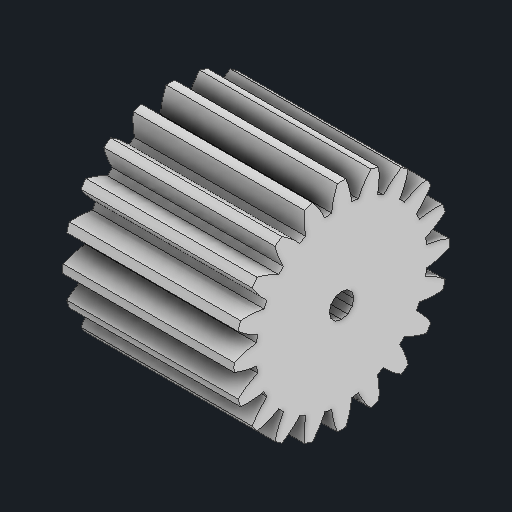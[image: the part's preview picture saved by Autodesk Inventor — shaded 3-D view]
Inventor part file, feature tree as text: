
AUTODESK INVENTOR PART (.ipt)
format: ipt  version: 2024 (Build 280153000, 153)  size: 380,928 bytes
history: native  units: mm
features: other x4, extrude x2, sketch x2, projected_geometry x1
ambient origin geometry x8: Origin, YZ Plane, XZ Plane, XY Plane, X Axis, Y Axis, Z Axis, Center Point
bodies: Body1 (feature_tree)
feature tree (9):
  other  "{BB8FE430-83BF-418D-8DF9-9B323D3DB9B9}"
  other  "솔리드1"
  extrude  "돌출1"  Depth=44.31mm
  other  "스퍼 기어 톱니1"
  extrude  "돌출2"  Depth=15.0mm TaperAngle=0.0deg
  sketch  "스케치1"
  other  "스퍼 기어1"
  sketch  "스케치2"
  projected_geometry  "투영된 루프1"
